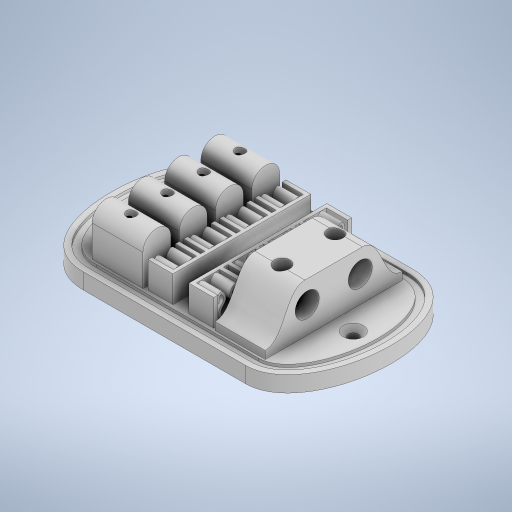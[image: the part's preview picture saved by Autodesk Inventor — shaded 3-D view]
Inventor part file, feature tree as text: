
AUTODESK INVENTOR PART (.ipt)
format: ipt  version: 2023 (Build 270158000, 158)  size: 817,664 bytes
history: native  units: in
note: dims shown in document units (in); Inventor stores cm internally (conversion verified against a paired STEP export)
features: extrude x10, sketch x9, plane x3, projected_geometry x3, mirror x1, pattern_linear x1, chamfer x1
ambient origin geometry x8: Origin, YZ Plane, XZ Plane, XY Plane, X Axis, Y Axis, Z Axis, Center Point
bodies: Body1 (feature_tree)
feature tree (28):
  extrude  "Extrusion2"  Depth=7.874in
  sketch  "Sketch4"  dims[d33=5.9055in d34=2.9528in]
  plane  "Work Plane1"
  sketch  "Sketch5"  dims[d35=3.937in d36=1.4862in]
  extrude  "Extrusion3"  Depth=2.9528in
  extrude  "Extrusion4"  Depth=1.4862in
  extrude  "Extrusion5"  Depth=0.9843in
  plane  "Work Plane2"
  extrude  "Extrusion6"  Depth=0.9843in
  plane  "Work Plane3"
  extrude  "Extrusion7"  Depth=0.1024in
  extrude  "Extrusion8"  Depth=1.5256in
  mirror  "Mirror1"
  sketch  "Sketch10"  dims[d41=0.2835in d42=0.0in d43=0.1024in]
  extrude  "Extrusion9"  Depth=2.4409in
  pattern_linear  "Rectangular Pattern1"  Spacing1=0.1378in  [1 undecoded]
  extrude  "Extrusion10"  Depth=1.0236in
  extrude  "Extrusion11"  Depth=0.5118in
  chamfer  "Chamfer1"  Distance=0.4272in
  sketch  "Sketch3"  dims[d31=2.9724in d32=7.874in]
  projected_geometry  "Projected Loop5"
  sketch  "Sketch6"  dims[d37=2.4272in d38=0.9843in]
  projected_geometry  "Projected Loop6"
  projected_geometry  "Projected Loop7"
  sketch  "Sketch9"  dims[d39=2.9724in d40=0.9843in]
  sketch  "Sketch11"  dims[d44=0.2264in d45=1.5256in]
  sketch  "Sketch12"  dims[d46=0.8701in d47=2.4409in]
  sketch  "Sketch13"  dims[d48=1.2205in d49=0.1378in d51=1.0236in d52=0.5118in d53=0.4272in d54=0.4724in d55=0.4724in d56=0.4006in d57=0.4006in d58=0.0492in d59=0.0in d60=0.8929in d61=0.0in d62=0.2756in d63=0.2756in d64=0.2756in d65=0.0in d66=1.2894in d67=0.498in d71=1.5748in d73=0.6457in d74=0.3937in d76=0.3937in d78=0.9055in d79=0.0in d80=0.7992in d81=0.1732in d86=1.5748in d88=0.6457in d89=0.3937in d91=0.3937in d93=0.2362in d94=0.0in d96=0.0709in d97=0.4134in d99=0.0787in d100=0.2913in d101=0.0472in d102=0.4429in d103=0.063in d104=0.3799in d105=0.4724in d106=0.0in d107=0.3543in d108=0.1181in d109=0.2362in d110=0.1181in d111=0.0591in d112=0.3543in d113=0.1772in d114=0.2362in d115=0.1181in d116=0.1772in d117=0.0886in d128=0.3543in d131=0.1181in d132=0.0787in d134=0.3543in d137=0.0197in d139=0.0197in d145=0.0197in d146=0.0197in d147=0.3543in d148=0.0in d149=1.5748in d151=0.6299in d152=0.7874in d154=0.7776in d155=0.5581in d156=0.315in d157=0.315in d158=0.315in d159=0.315in d160=0.3937in d161=0.0in d162=0.1772in d163=0.1772in d164=3.752in d165=1.876in d166=0.3937in d167=0.0in d168=0.0886in d169=0.0787in d170=45.0deg]
note: 1 required parameter value undecoded (feature->parameter linkage not recoverable at this tier; creation-order binding heuristic only, values carry confidence <= 0.55)
